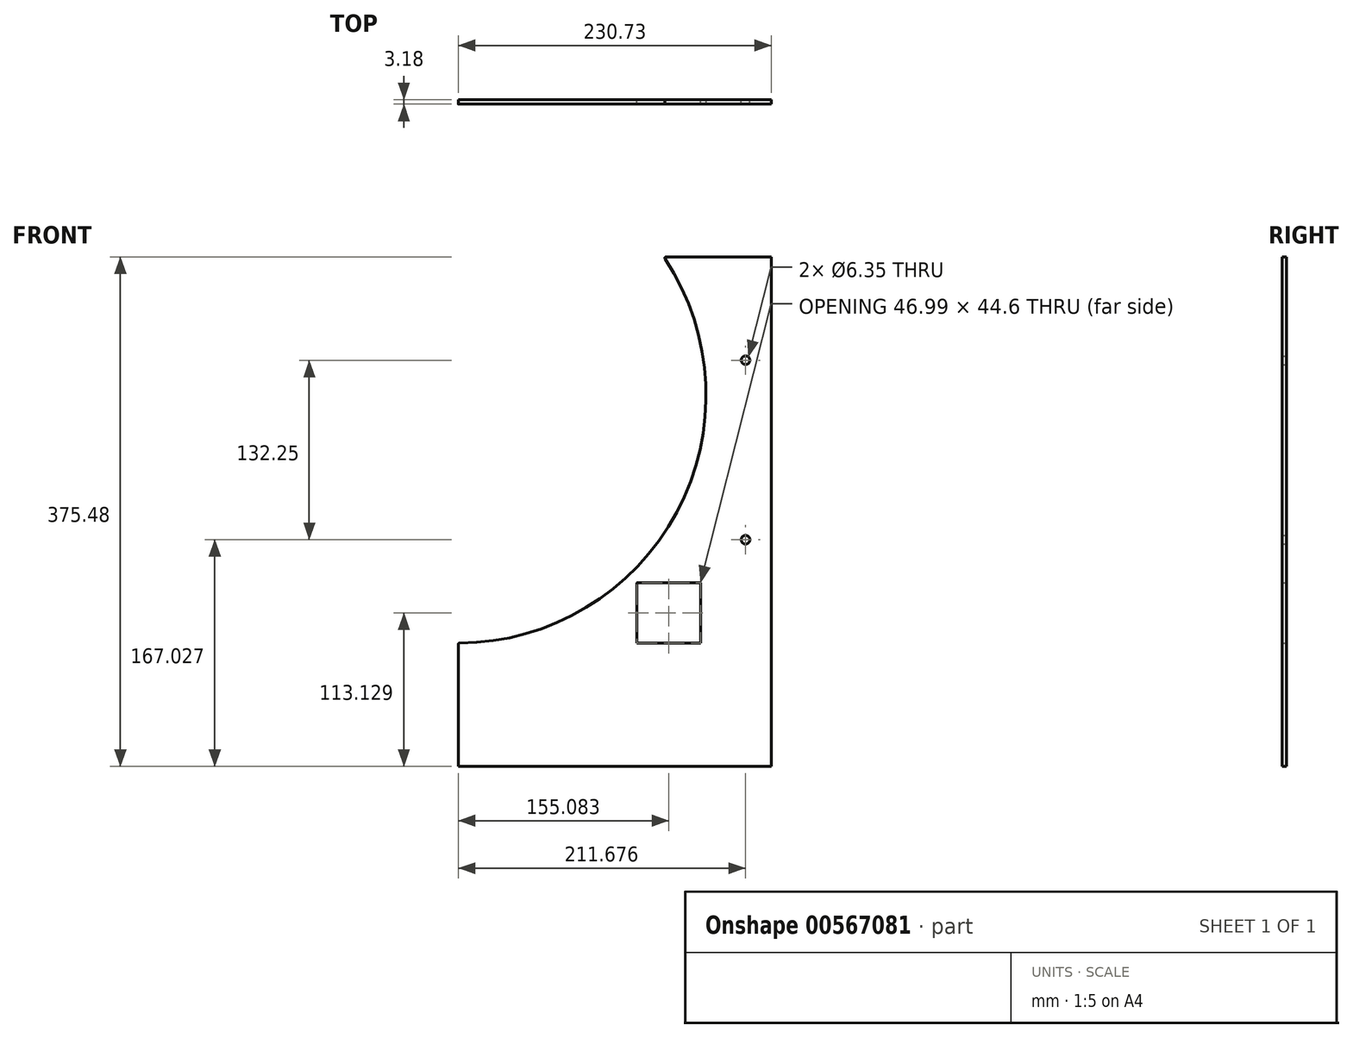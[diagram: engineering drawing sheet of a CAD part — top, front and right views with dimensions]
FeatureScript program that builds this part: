
annotation { "Feature Type Name" : "Feature", "Feature Type Description" : "" }
export const myFeature = defineFeature(function(context is Context, id is Id, definition is map)
    precondition{}
    {
        {
            var Q0;
            Q0=qCreatedBy(makeId("Front.planeOp"),FACE);
            var sketch = newSketch(context, id + "F0", { "sketchPlane" : qUnion([Q0])});
            skArc(sketch, "E0", {"start": v(0, -182.56) * mm, "mid": v(161.2, -85.7) * mm, "end": v(151.35, 102.09) * mm});
            skCircle(sketch, "E1", {"center": v(0, 0) * mm, "radius": 61.91 * mm, "construction": true});
            skLineSegment(sketch, "E2", {"start": v(0, 0) * mm, "end": v(0, -298.83) * mm, "construction": true});
            skLineSegment(sketch, "E3", {"start": v(0, -182.56) * mm, "end": v(131.59, -182.56) * mm, "construction": true});
            skLineSegment(sketch, "E4", {"start": v(230.73, -182.56) * mm, "end": v(230.73, 102.09) * mm});
            skLineSegment(sketch, "E5", {"start": v(230.73, 102.09) * mm, "end": v(151.35, 102.09) * mm});
            skLineSegment(sketch, "E6", {"start": v(0, 0) * mm, "end": v(377.6, 0) * mm, "construction": true});
            skLineSegment(sketch, "E7", {"start": v(182.56, 0) * mm, "end": v(151.35, 102.09) * mm, "construction": true});
            skLineSegment(sketch, "E8", {"start": v(182.56, 0) * mm, "end": v(182.56, 254) * mm, "construction": true});
            skCircle(sketch, "E9", {"center": v(173.38, 82.7) * mm, "radius": 3.18 * mm, "construction": true});
            skCircle(sketch, "E10.1.0", {"center": v(191.56, 14.24) * mm, "radius": 3.18 * mm, "construction": true});
            skCircle(sketch, "E10.2.0", {"center": v(183.7, -56.16) * mm, "radius": 3.18 * mm, "construction": true});
            skCircle(sketch, "E10.3.0", {"center": v(150.85, -118.92) * mm, "radius": 3.18 * mm, "construction": true});
            skCircle(sketch, "E10.4.0", {"center": v(97.5, -165.5) * mm, "radius": 3.18 * mm, "construction": true});
            skLineSegment(sketch, "E10.anchor1", {"start": v(0, 0) * mm, "end": v(173.38, 82.7) * mm, "construction": true});
            skLineSegment(sketch, "E10.anchor2", {"start": v(0, 0) * mm, "end": v(97.5, -165.5) * mm, "construction": true});
            skLineSegment(sketch, "E11.bottom", {"start": v(132.22, -137.96) * mm, "end": v(177.94, -137.96) * mm});
            skLineSegment(sketch, "E11.left", {"start": v(131.59, -138.6) * mm, "end": v(131.59, -182.56) * mm});
            skLineSegment(sketch, "E11.right", {"start": v(178.58, -138.6) * mm, "end": v(178.58, -182.56) * mm});
            skLineSegment(sketch, "E12", {"start": v(155.08, -137.96) * mm, "end": v(155.08, -182.56) * mm, "construction": true});
            skPoint(sketch, "E13", {"position": v(155.08, -160.26) * mm});
            skLineSegment(sketch, "E14.trimOffspring", {"start": v(178.58, -182.56) * mm, "end": v(230.73, -182.56) * mm, "construction": true});
            skPoint(sketch, "E15.visualSharp", {"position": v(131.59, -137.96) * mm});
            skArc(sketch, "E15.filletArc", {"start": v(132.22, -137.96) * mm, "mid": v(131.77, -138.15) * mm, "end": v(131.59, -138.6) * mm});
            skPoint(sketch, "E16.visualSharp", {"position": v(178.58, -137.96) * mm});
            skArc(sketch, "E16.filletArc", {"start": v(178.58, -138.6) * mm, "mid": v(178.4, -138.15) * mm, "end": v(177.94, -137.96) * mm});
            skLineSegment(sketch, "E17", {"start": v(211.68, 102.09) * mm, "end": v(211.68, -182.56) * mm, "construction": true});
            skLineSegment(sketch, "E18", {"start": v(230.73, 25.89) * mm, "end": v(180.72, 25.89) * mm, "construction": true});
            skLineSegment(sketch, "E19", {"start": v(148.38, -106.36) * mm, "end": v(230.73, -106.36) * mm, "construction": true});
            skCircle(sketch, "E20", {"center": v(211.68, -106.36) * mm, "radius": 3.18 * mm});
            skCircle(sketch, "E21", {"center": v(211.68, 25.89) * mm, "radius": 3.18 * mm});
            skLineSegment(sketch, "E22", {"start": v(0, 0) * mm, "end": v(151.35, 102.09) * mm, "construction": true});
            skLineSegment(sketch, "E23", {"start": v(0, -182.56) * mm, "end": v(0, -273.4) * mm});
            skLineSegment(sketch, "E24", {"start": v(0, -273.4) * mm, "end": v(230.73, -273.4) * mm});
            skLineSegment(sketch, "E25", {"start": v(230.73, -273.4) * mm, "end": v(230.73, -182.56) * mm});
            skLineSegment(sketch, "E26", {"start": v(131.59, -182.56) * mm, "end": v(178.58, -182.56) * mm});
            skSolve(sketch);
        }
        {
            var Q0;
            Q0=qSketchRegion(id+"F0",true);
            extrude(context, id + "F1", {"entities" : qUnion([Q0]), "depth" : 3.17 * mm});
        }
        {
            var Q0;
            Q0=makeQuery(id+"F1.opExtrude","CAP_FACE",FACE,{"disambiguationData":[OSD([sQuery(id+"F0.wireOp",EDGE,"E0"),sQuery(id+"F0.wireOp",EDGE,"E3"),sQuery(id+"F0.wireOp",EDGE,"E4"),sQuery(id+"F0.wireOp",EDGE,"E5"),sQuery(id+"F0.wireOp",EDGE,"E11.bottom"),sQuery(id+"F0.wireOp",EDGE,"E11.left"),sQuery(id+"F0.wireOp",EDGE,"E11.right"),sQuery(id+"F0.wireOp",EDGE,"E14.trimOffspring"),sQuery(id+"F0.wireOp",EDGE,"E15.filletArc"),sQuery(id+"F0.wireOp",EDGE,"E16.filletArc")])],"isStart":false});
            var sketch = newSketch(context, id + "F2", { "sketchPlane" : qUnion([Q0])});
            skLineSegment(sketch, "E27", {"start": v(86.22, -160.92) * mm, "end": v(87, -162.32) * mm});
            skLineSegment(sketch, "E28", {"start": v(87, -162.32) * mm, "end": v(84.93, -163.45) * mm});
            skLineSegment(sketch, "E29", {"start": v(84.93, -163.45) * mm, "end": v(86.58, -166.46) * mm});
            skLineSegment(sketch, "E30", {"start": v(86.58, -166.46) * mm, "end": v(88.64, -165.33) * mm});
            skLineSegment(sketch, "E31", {"start": v(88.64, -165.33) * mm, "end": v(89.52, -166.93) * mm});
            skLineSegment(sketch, "E32", {"start": v(89.52, -166.93) * mm, "end": v(92.64, -165.22) * mm});
            skLineSegment(sketch, "E33", {"start": v(92.64, -165.22) * mm, "end": v(91.76, -163.62) * mm});
            skLineSegment(sketch, "E34", {"start": v(91.76, -163.62) * mm, "end": v(93.82, -162.49) * mm});
            skLineSegment(sketch, "E35", {"start": v(93.82, -162.49) * mm, "end": v(92.17, -159.48) * mm});
            skLineSegment(sketch, "E36", {"start": v(92.17, -159.48) * mm, "end": v(90.11, -160.61) * mm});
            skLineSegment(sketch, "E37", {"start": v(90.11, -160.61) * mm, "end": v(89.34, -159.2) * mm});
            skLineSegment(sketch, "E38", {"start": v(164.06, 80.1) * mm, "end": v(165.5, 80.78) * mm});
            skLineSegment(sketch, "E39", {"start": v(165.5, 80.78) * mm, "end": v(164.49, 82.9) * mm});
            skLineSegment(sketch, "E40", {"start": v(164.49, 82.9) * mm, "end": v(167.59, 84.38) * mm});
            skLineSegment(sketch, "E41", {"start": v(167.59, 84.38) * mm, "end": v(168.6, 82.26) * mm});
            skLineSegment(sketch, "E42", {"start": v(168.6, 82.26) * mm, "end": v(170.25, 83.04) * mm});
            skLineSegment(sketch, "E43", {"start": v(170.25, 83.04) * mm, "end": v(171.78, 79.83) * mm});
            skLineSegment(sketch, "E44", {"start": v(171.78, 79.83) * mm, "end": v(170.12, 79.04) * mm});
            skLineSegment(sketch, "E45", {"start": v(170.12, 79.04) * mm, "end": v(171.14, 76.92) * mm});
            skLineSegment(sketch, "E46", {"start": v(171.14, 76.92) * mm, "end": v(168.04, 75.45) * mm});
            skLineSegment(sketch, "E47", {"start": v(168.04, 75.45) * mm, "end": v(167.03, 77.57) * mm});
            skLineSegment(sketch, "E48", {"start": v(167.03, 77.57) * mm, "end": v(165.58, 76.88) * mm});
            skSolve(sketch);
        }
        {
            var Q0;
            Q0=makeQuery(id+"F1.opExtrude","SWEPT_EDGE",EDGE,{"disambiguationData":[OSD([sQuery(id+"F0.wireOp",EDGE,"E0"),sQuery(id+"F0.wireOp",EDGE,"E5")])]});
            var Q1;
            Q1=makeQuery(id+"F1.opExtrude","SWEPT_EDGE",EDGE,{"disambiguationData":[OSD([sQuery(id+"F0.wireOp",EDGE,"E0"),sQuery(id+"F0.wireOp",EDGE,"E3")])]});
            fillet(context, id + "F3", {"entities" : qUnion([Q0, Q1]), "radius" : 1.02 * mm, "tangentPropagation" : true, "allowEdgeOverflow" : false});
        }
    });
